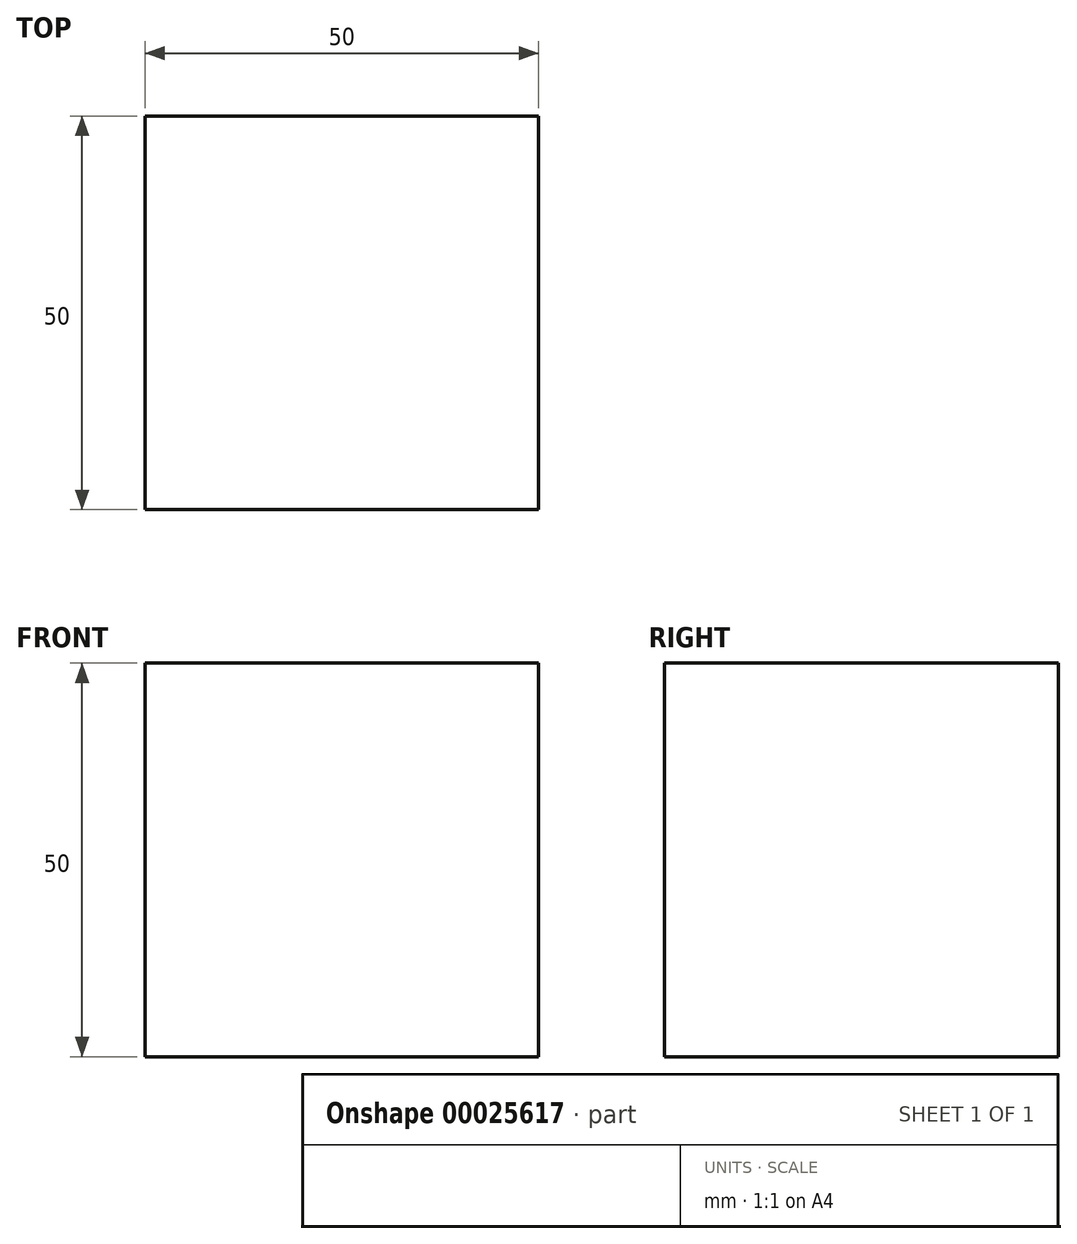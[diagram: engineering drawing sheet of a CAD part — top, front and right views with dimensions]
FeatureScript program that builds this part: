
annotation { "Feature Type Name" : "Feature", "Feature Type Description" : "" }
export const myFeature = defineFeature(function(context is Context, id is Id, definition is map)
    precondition{}
    {
        {
            var Q0;
            Q0=qCreatedBy(makeId("Top.planeOp"),FACE);
            var sketch = newSketch(context, id + "F0", { "sketchPlane" : qUnion([Q0])});
            skLineSegment(sketch, "E0.bottom", {"start": v(-5.8, 43.76) * mm, "end": v(44.2, 43.76) * mm});
            skLineSegment(sketch, "E0.top", {"start": v(-5.8, -6.24) * mm, "end": v(44.2, -6.24) * mm});
            skLineSegment(sketch, "E0.left", {"start": v(-5.8, 43.76) * mm, "end": v(-5.8, -6.24) * mm});
            skLineSegment(sketch, "E0.right", {"start": v(44.2, 43.76) * mm, "end": v(44.2, -6.24) * mm});
            skSolve(sketch);
        }
        {
            var Q0;
            Q0=makeQuery(id+"F0.imprint","IMPRINT",FACE,{"disambiguationData":[TD([[makeQuery(id+"F0.imprint","IMPRINT",EDGE,{"derivedFrom":sQuery(id+"F0.wireOp",EDGE,"E0.bottom")}),-1.0]])]});
            extrude(context, id + "F1", {"entities" : qUnion([Q0]), "depth" : 50 * mm});
        }
    });
